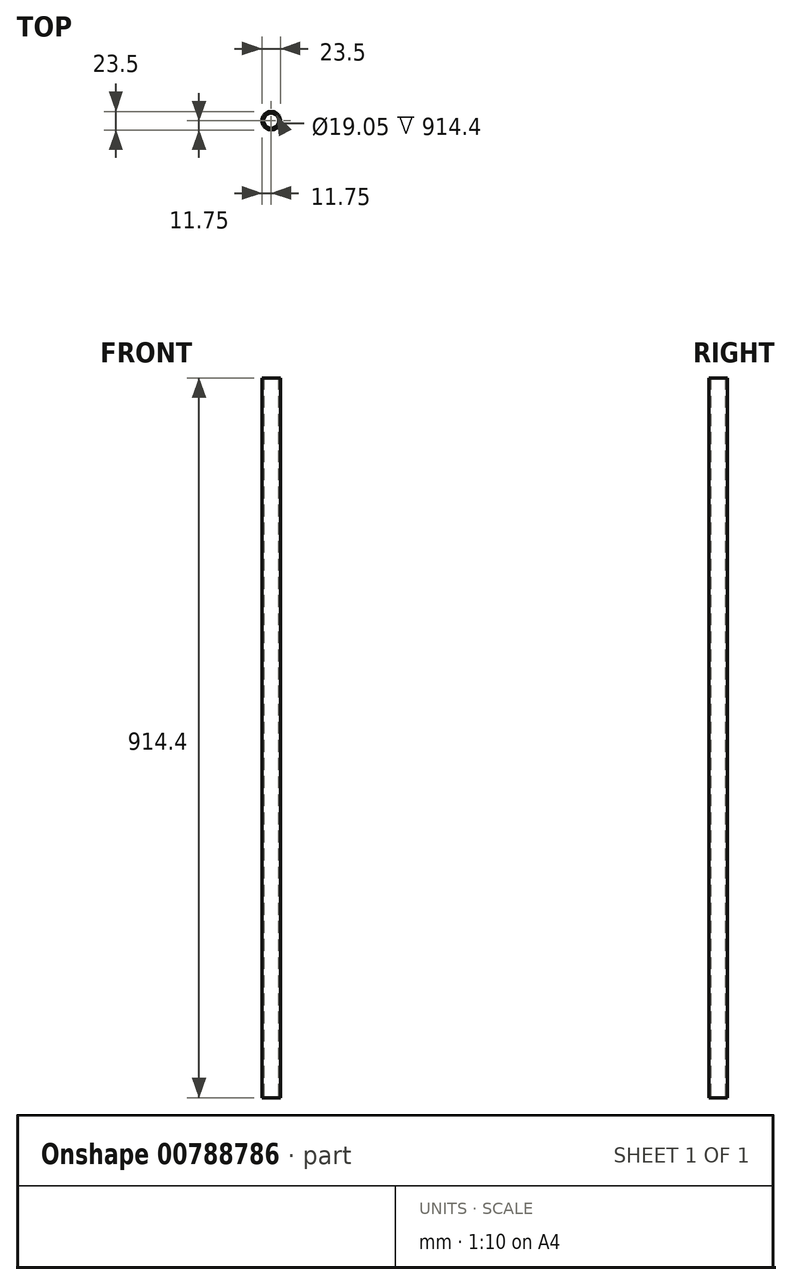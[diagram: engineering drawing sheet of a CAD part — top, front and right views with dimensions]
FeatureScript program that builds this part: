
annotation { "Feature Type Name" : "Feature", "Feature Type Description" : "" }
export const myFeature = defineFeature(function(context is Context, id is Id, definition is map)
    precondition{}
    {
        {
            var Q0;
            Q0=qCreatedBy(makeId("Top.planeOp"),FACE);
            var sketch = newSketch(context, id + "F0", { "sketchPlane" : qUnion([Q0])});
            skCircle(sketch, "E0", {"center": v(0, 0) * mm, "radius": 9.52 * mm});
            skCircle(sketch, "E1", {"center": v(0, 0) * mm, "radius": 11.75 * mm});
            skSolve(sketch);
        }
        {
            var Q0;
            Q0=makeQuery(id+"F0.imprint","IMPRINT",FACE,{"disambiguationData":[TD([[makeQuery(id+"F0.imprint","IMPRINT",EDGE,{"derivedFrom":sQuery(id+"F0.wireOp",EDGE,"E0")}),-1.0]])]});
            extrude(context, id + "F1", {"entities" : qUnion([Q0]), "depth" : (36 * 25.4) * mm, "offsetDistance" : 25 * mm});
        }
    });
